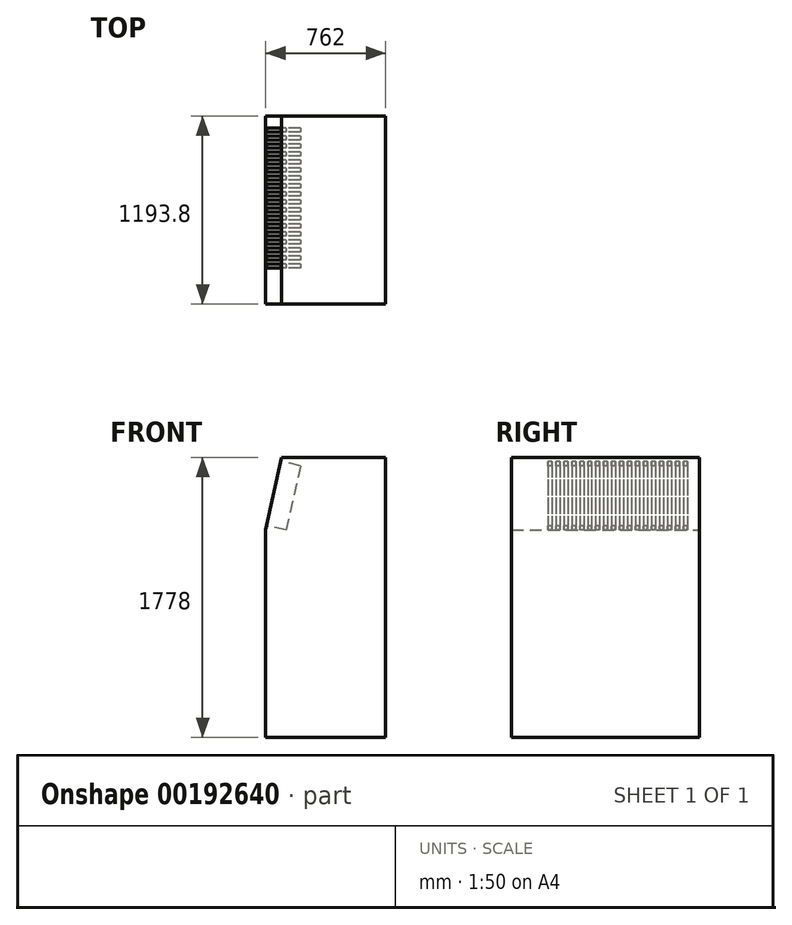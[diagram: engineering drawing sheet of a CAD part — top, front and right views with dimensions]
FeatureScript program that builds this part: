
annotation { "Feature Type Name" : "Feature", "Feature Type Description" : "" }
export const myFeature = defineFeature(function(context is Context, id is Id, definition is map)
    precondition{}
    {
        {
            var Q0;
            Q0=qCreatedBy(makeId("Front.planeOp"),FACE);
            var sketch = newSketch(context, id + "F0", { "sketchPlane" : qUnion([Q0])});
            skLineSegment(sketch, "E0.bottom", {"start": v(-381, 889) * mm, "end": v(381, 889) * mm});
            skLineSegment(sketch, "E0.top", {"start": v(-381, -889) * mm, "end": v(381, -889) * mm});
            skLineSegment(sketch, "E0.left", {"start": v(-381, 889) * mm, "end": v(-381, -889) * mm});
            skLineSegment(sketch, "E0.right", {"start": v(381, 889) * mm, "end": v(381, -889) * mm});
            skSolve(sketch);
        }
        {
            var Q0;
            Q0=makeQuery(id+"F0.imprint","IMPRINT",FACE,{"disambiguationData":[TD([[makeQuery(id+"F0.imprint","IMPRINT",EDGE,{"derivedFrom":sQuery(id+"F0.wireOp",EDGE,"E0.bottom")}),-1.0]])]});
            extrude(context, id + "F1", {"entities" : qUnion([Q0]), "depth" : 1193.8 * mm});
        }
        {
            var Q0;
            Q0=makeQuery(id+"F1.opExtrude","CAP_FACE",FACE,{"disambiguationData":[OSD([sQuery(id+"F0.wireOp",EDGE,"E0.bottom"),sQuery(id+"F0.wireOp",EDGE,"E0.top"),sQuery(id+"F0.wireOp",EDGE,"E0.left"),sQuery(id+"F0.wireOp",EDGE,"E0.right")])],"isStart":true});
            var sketch = newSketch(context, id + "F2", { "sketchPlane" : qUnion([Q0])});
            skLineSegment(sketch, "E1", {"start": v(279.4, 889) * mm, "end": v(381, 430.12) * mm});
            skSolve(sketch);
        }
        {
            var Q0;
            {var subQ0=sQuery(id+"F2.wireOp",EDGE,"E1");Q0=makeQuery(id+"F2.imprint","IMPRINT",FACE,{"disambiguationData":[TD([[makeQuery(id+"F2.imprint","IMPRINT",EDGE,{"derivedFrom":subQ0}),1.0]])]});}
            extrude(context, id + "F3", {"entities" : qUnion([Q0]), "operationType" : NewBodyOperationType.REMOVE, "oppositeDirection" : true, "depth" : 1524 * mm});
        }
        {
            var Q0;
            Q0=makeQuery(id+"F3.boolean.opBoolean","COPY",FACE,{"derivedFrom":makeQuery(id+"F3.opExtrude","SWEPT_FACE",FACE,{"disambiguationData":[OSD([sQuery(id+"F2.wireOp",EDGE,"E1")])]})});
            var sketch = newSketch(context, id + "F4", { "sketchPlane" : qUnion([Q0])});
            skLineSegment(sketch, "E2.bottom", {"start": v(76.2, 782.18) * mm, "end": v(1117.6, 782.18) * mm});
            skLineSegment(sketch, "E2.top", {"start": v(76.2, 362.99) * mm, "end": v(1117.6, 362.99) * mm});
            skLineSegment(sketch, "E2.left", {"start": v(76.2, 782.18) * mm, "end": v(76.2, 362.99) * mm});
            skLineSegment(sketch, "E2.right", {"start": v(1117.6, 782.18) * mm, "end": v(1117.6, 362.99) * mm});
            skLineSegment(sketch, "E3.bottom", {"start": v(101.6, 782.18) * mm, "end": v(127, 782.18) * mm});
            skLineSegment(sketch, "E3.top", {"start": v(101.6, 362.99) * mm, "end": v(127, 362.99) * mm});
            skLineSegment(sketch, "E3.left", {"start": v(101.6, 782.18) * mm, "end": v(101.6, 362.99) * mm});
            skLineSegment(sketch, "E3.right", {"start": v(127, 782.18) * mm, "end": v(127, 362.99) * mm});
            skLineSegment(sketch, "E4.bottom", {"start": v(152.4, 782.18) * mm, "end": v(177.8, 782.18) * mm});
            skLineSegment(sketch, "E4.top", {"start": v(152.4, 362.99) * mm, "end": v(177.8, 362.99) * mm});
            skLineSegment(sketch, "E4.left", {"start": v(152.4, 782.18) * mm, "end": v(152.4, 362.99) * mm});
            skLineSegment(sketch, "E4.right", {"start": v(177.8, 782.18) * mm, "end": v(177.8, 362.99) * mm});
            skLineSegment(sketch, "E5.bottom", {"start": v(203.2, 782.18) * mm, "end": v(228.6, 782.18) * mm});
            skLineSegment(sketch, "E5.top", {"start": v(203.2, 362.99) * mm, "end": v(228.6, 362.99) * mm});
            skLineSegment(sketch, "E5.left", {"start": v(203.2, 782.18) * mm, "end": v(203.2, 362.99) * mm});
            skLineSegment(sketch, "E5.right", {"start": v(228.6, 782.18) * mm, "end": v(228.6, 362.99) * mm});
            skLineSegment(sketch, "E6.bottom", {"start": v(254, 782.18) * mm, "end": v(279.4, 782.18) * mm});
            skLineSegment(sketch, "E6.top", {"start": v(254, 362.99) * mm, "end": v(279.4, 362.99) * mm});
            skLineSegment(sketch, "E6.left", {"start": v(254, 782.18) * mm, "end": v(254, 362.99) * mm});
            skLineSegment(sketch, "E6.right", {"start": v(279.4, 782.18) * mm, "end": v(279.4, 362.99) * mm});
            skLineSegment(sketch, "E7.bottom", {"start": v(304.8, 782.18) * mm, "end": v(330.2, 782.18) * mm});
            skLineSegment(sketch, "E7.top", {"start": v(304.8, 362.99) * mm, "end": v(330.2, 362.99) * mm});
            skLineSegment(sketch, "E7.left", {"start": v(304.8, 782.18) * mm, "end": v(304.8, 362.99) * mm});
            skLineSegment(sketch, "E7.right", {"start": v(330.2, 782.18) * mm, "end": v(330.2, 362.99) * mm});
            skLineSegment(sketch, "E8.bottom", {"start": v(355.6, 782.18) * mm, "end": v(381, 782.18) * mm});
            skLineSegment(sketch, "E8.top", {"start": v(355.6, 362.99) * mm, "end": v(381, 362.99) * mm});
            skLineSegment(sketch, "E8.left", {"start": v(355.6, 782.18) * mm, "end": v(355.6, 362.99) * mm});
            skLineSegment(sketch, "E8.right", {"start": v(381, 782.18) * mm, "end": v(381, 362.99) * mm});
            skLineSegment(sketch, "E9.bottom", {"start": v(406.4, 782.18) * mm, "end": v(431.8, 782.18) * mm});
            skLineSegment(sketch, "E9.top", {"start": v(406.4, 362.99) * mm, "end": v(431.8, 362.99) * mm});
            skLineSegment(sketch, "E9.left", {"start": v(406.4, 782.18) * mm, "end": v(406.4, 362.99) * mm});
            skLineSegment(sketch, "E9.right", {"start": v(431.8, 782.18) * mm, "end": v(431.8, 362.99) * mm});
            skLineSegment(sketch, "E10.bottom", {"start": v(457.2, 782.18) * mm, "end": v(482.6, 782.18) * mm});
            skLineSegment(sketch, "E10.top", {"start": v(457.2, 362.99) * mm, "end": v(482.6, 362.99) * mm});
            skLineSegment(sketch, "E10.left", {"start": v(457.2, 782.18) * mm, "end": v(457.2, 362.99) * mm});
            skLineSegment(sketch, "E10.right", {"start": v(482.6, 782.18) * mm, "end": v(482.6, 362.99) * mm});
            skLineSegment(sketch, "E11.bottom", {"start": v(508, 782.18) * mm, "end": v(533.4, 782.18) * mm});
            skLineSegment(sketch, "E11.top", {"start": v(508, 362.99) * mm, "end": v(533.4, 362.99) * mm});
            skLineSegment(sketch, "E11.left", {"start": v(508, 782.18) * mm, "end": v(508, 362.99) * mm});
            skLineSegment(sketch, "E11.right", {"start": v(533.4, 782.18) * mm, "end": v(533.4, 362.99) * mm});
            skLineSegment(sketch, "E12.bottom", {"start": v(558.8, 782.18) * mm, "end": v(584.2, 782.18) * mm});
            skLineSegment(sketch, "E12.top", {"start": v(558.8, 362.99) * mm, "end": v(584.2, 362.99) * mm});
            skLineSegment(sketch, "E12.left", {"start": v(558.8, 782.18) * mm, "end": v(558.8, 362.99) * mm});
            skLineSegment(sketch, "E12.right", {"start": v(584.2, 782.18) * mm, "end": v(584.2, 362.99) * mm});
            skLineSegment(sketch, "E13.bottom", {"start": v(609.6, 782.18) * mm, "end": v(635, 782.18) * mm});
            skLineSegment(sketch, "E13.top", {"start": v(609.6, 362.99) * mm, "end": v(635, 362.99) * mm});
            skLineSegment(sketch, "E13.left", {"start": v(609.6, 782.18) * mm, "end": v(609.6, 362.99) * mm});
            skLineSegment(sketch, "E13.right", {"start": v(635, 782.18) * mm, "end": v(635, 362.99) * mm});
            skLineSegment(sketch, "E14.bottom", {"start": v(660.4, 782.18) * mm, "end": v(685.8, 782.18) * mm});
            skLineSegment(sketch, "E14.top", {"start": v(660.4, 362.99) * mm, "end": v(685.8, 362.99) * mm});
            skLineSegment(sketch, "E14.left", {"start": v(660.4, 782.18) * mm, "end": v(660.4, 362.99) * mm});
            skLineSegment(sketch, "E14.right", {"start": v(685.8, 782.18) * mm, "end": v(685.8, 362.99) * mm});
            skLineSegment(sketch, "E15.bottom", {"start": v(710.97, 782.18) * mm, "end": v(736.37, 782.18) * mm});
            skLineSegment(sketch, "E15.top", {"start": v(710.97, 362.99) * mm, "end": v(736.37, 362.99) * mm});
            skLineSegment(sketch, "E15.left", {"start": v(710.97, 782.18) * mm, "end": v(710.97, 362.99) * mm});
            skLineSegment(sketch, "E15.right", {"start": v(736.37, 782.18) * mm, "end": v(736.37, 362.99) * mm});
            skLineSegment(sketch, "E16.bottom", {"start": v(761.77, 782.18) * mm, "end": v(787.17, 782.18) * mm});
            skLineSegment(sketch, "E16.top", {"start": v(761.77, 362.99) * mm, "end": v(787.17, 362.99) * mm});
            skLineSegment(sketch, "E16.left", {"start": v(761.77, 782.18) * mm, "end": v(761.77, 362.99) * mm});
            skLineSegment(sketch, "E16.right", {"start": v(787.17, 782.18) * mm, "end": v(787.17, 362.99) * mm});
            skLineSegment(sketch, "E17.bottom", {"start": v(812.57, 782.18) * mm, "end": v(837.97, 782.18) * mm});
            skLineSegment(sketch, "E17.top", {"start": v(812.57, 362.99) * mm, "end": v(837.97, 362.99) * mm});
            skLineSegment(sketch, "E17.left", {"start": v(812.57, 782.18) * mm, "end": v(812.57, 362.99) * mm});
            skLineSegment(sketch, "E17.right", {"start": v(837.97, 782.18) * mm, "end": v(837.97, 362.99) * mm});
            skLineSegment(sketch, "E18.bottom", {"start": v(863.37, 782.18) * mm, "end": v(888.77, 782.18) * mm});
            skLineSegment(sketch, "E18.top", {"start": v(863.37, 362.99) * mm, "end": v(888.77, 362.99) * mm});
            skLineSegment(sketch, "E18.left", {"start": v(863.37, 782.18) * mm, "end": v(863.37, 362.99) * mm});
            skLineSegment(sketch, "E18.right", {"start": v(888.77, 782.18) * mm, "end": v(888.77, 362.99) * mm});
            skLineSegment(sketch, "E19.bottom", {"start": v(914.17, 782.18) * mm, "end": v(939.57, 782.18) * mm});
            skLineSegment(sketch, "E19.top", {"start": v(914.17, 362.99) * mm, "end": v(939.57, 362.99) * mm});
            skLineSegment(sketch, "E19.left", {"start": v(914.17, 782.18) * mm, "end": v(914.17, 362.99) * mm});
            skLineSegment(sketch, "E19.right", {"start": v(939.57, 782.18) * mm, "end": v(939.57, 362.99) * mm});
            skLineSegment(sketch, "E20.bottom", {"start": v(964.97, 782.18) * mm, "end": v(990.37, 782.18) * mm});
            skLineSegment(sketch, "E20.top", {"start": v(964.97, 362.99) * mm, "end": v(990.37, 362.99) * mm});
            skLineSegment(sketch, "E20.left", {"start": v(964.97, 782.18) * mm, "end": v(964.97, 362.99) * mm});
            skLineSegment(sketch, "E20.right", {"start": v(990.37, 782.18) * mm, "end": v(990.37, 362.99) * mm});
            skLineSegment(sketch, "E21.bottom", {"start": v(1005.12, 782.18) * mm, "end": v(1030.52, 782.18) * mm});
            skLineSegment(sketch, "E21.top", {"start": v(1005.12, 362.99) * mm, "end": v(1030.52, 362.99) * mm});
            skLineSegment(sketch, "E21.left", {"start": v(1005.12, 782.18) * mm, "end": v(1005.12, 362.99) * mm});
            skLineSegment(sketch, "E21.right", {"start": v(1030.52, 782.18) * mm, "end": v(1030.52, 362.99) * mm});
            skLineSegment(sketch, "E22.bottom", {"start": v(1055.92, 782.18) * mm, "end": v(1081.32, 782.18) * mm});
            skLineSegment(sketch, "E22.top", {"start": v(1055.92, 362.99) * mm, "end": v(1081.32, 362.99) * mm});
            skLineSegment(sketch, "E22.left", {"start": v(1055.92, 782.18) * mm, "end": v(1055.92, 362.99) * mm});
            skLineSegment(sketch, "E22.right", {"start": v(1081.32, 782.18) * mm, "end": v(1081.32, 362.99) * mm});
            skSolve(sketch);
        }
        {
            var Q0;
            {var subQ0=sQuery(id+"F4.wireOp",EDGE,"E2.left");Q0=makeQuery(id+"F4.imprint","IMPRINT",FACE,{"disambiguationData":[TD([[makeQuery(id+"F4.imprint","IMPRINT",EDGE,{"derivedFrom":subQ0}),1.0]])]});}
            var Q1;
            {var subQ0=sQuery(id+"F4.wireOp",EDGE,"E3.right");Q1=makeQuery(id+"F4.imprint","IMPRINT",FACE,{"disambiguationData":[TD([[makeQuery(id+"F4.imprint","IMPRINT",EDGE,{"derivedFrom":subQ0}),1.0]])]});}
            var Q2;
            {var subQ0=sQuery(id+"F4.wireOp",EDGE,"E4.right");Q2=makeQuery(id+"F4.imprint","IMPRINT",FACE,{"disambiguationData":[TD([[makeQuery(id+"F4.imprint","IMPRINT",EDGE,{"derivedFrom":subQ0}),1.0]])]});}
            var Q3;
            {var subQ0=sQuery(id+"F4.wireOp",EDGE,"E5.right");Q3=makeQuery(id+"F4.imprint","IMPRINT",FACE,{"disambiguationData":[TD([[makeQuery(id+"F4.imprint","IMPRINT",EDGE,{"derivedFrom":subQ0}),1.0]])]});}
            var Q4;
            {var subQ0=sQuery(id+"F4.wireOp",EDGE,"E6.right");Q4=makeQuery(id+"F4.imprint","IMPRINT",FACE,{"disambiguationData":[TD([[makeQuery(id+"F4.imprint","IMPRINT",EDGE,{"derivedFrom":subQ0}),1.0]])]});}
            var Q5;
            {var subQ0=sQuery(id+"F4.wireOp",EDGE,"E7.right");Q5=makeQuery(id+"F4.imprint","IMPRINT",FACE,{"disambiguationData":[TD([[makeQuery(id+"F4.imprint","IMPRINT",EDGE,{"derivedFrom":subQ0}),1.0]])]});}
            var Q6;
            {var subQ0=sQuery(id+"F4.wireOp",EDGE,"E8.right");Q6=makeQuery(id+"F4.imprint","IMPRINT",FACE,{"disambiguationData":[TD([[makeQuery(id+"F4.imprint","IMPRINT",EDGE,{"derivedFrom":subQ0}),1.0]])]});}
            var Q7;
            {var subQ0=sQuery(id+"F4.wireOp",EDGE,"E9.right");Q7=makeQuery(id+"F4.imprint","IMPRINT",FACE,{"disambiguationData":[TD([[makeQuery(id+"F4.imprint","IMPRINT",EDGE,{"derivedFrom":subQ0}),1.0]])]});}
            var Q8;
            {var subQ0=sQuery(id+"F4.wireOp",EDGE,"E10.right");Q8=makeQuery(id+"F4.imprint","IMPRINT",FACE,{"disambiguationData":[TD([[makeQuery(id+"F4.imprint","IMPRINT",EDGE,{"derivedFrom":subQ0}),1.0]])]});}
            var Q9;
            {var subQ0=sQuery(id+"F4.wireOp",EDGE,"E11.right");Q9=makeQuery(id+"F4.imprint","IMPRINT",FACE,{"disambiguationData":[TD([[makeQuery(id+"F4.imprint","IMPRINT",EDGE,{"derivedFrom":subQ0}),1.0]])]});}
            var Q10;
            {var subQ0=sQuery(id+"F4.wireOp",EDGE,"E12.right");Q10=makeQuery(id+"F4.imprint","IMPRINT",FACE,{"disambiguationData":[TD([[makeQuery(id+"F4.imprint","IMPRINT",EDGE,{"derivedFrom":subQ0}),1.0]])]});}
            var Q11;
            {var subQ0=sQuery(id+"F4.wireOp",EDGE,"E13.right");Q11=makeQuery(id+"F4.imprint","IMPRINT",FACE,{"disambiguationData":[TD([[makeQuery(id+"F4.imprint","IMPRINT",EDGE,{"derivedFrom":subQ0}),1.0]])]});}
            var Q12;
            {var subQ0=sQuery(id+"F4.wireOp",EDGE,"E14.right");Q12=makeQuery(id+"F4.imprint","IMPRINT",FACE,{"disambiguationData":[TD([[makeQuery(id+"F4.imprint","IMPRINT",EDGE,{"derivedFrom":subQ0}),1.0]])]});}
            var Q13;
            {var subQ0=sQuery(id+"F4.wireOp",EDGE,"E15.right");Q13=makeQuery(id+"F4.imprint","IMPRINT",FACE,{"disambiguationData":[TD([[makeQuery(id+"F4.imprint","IMPRINT",EDGE,{"derivedFrom":subQ0}),1.0]])]});}
            var Q14;
            {var subQ0=sQuery(id+"F4.wireOp",EDGE,"E16.right");Q14=makeQuery(id+"F4.imprint","IMPRINT",FACE,{"disambiguationData":[TD([[makeQuery(id+"F4.imprint","IMPRINT",EDGE,{"derivedFrom":subQ0}),1.0]])]});}
            var Q15;
            {var subQ0=sQuery(id+"F4.wireOp",EDGE,"E17.right");Q15=makeQuery(id+"F4.imprint","IMPRINT",FACE,{"disambiguationData":[TD([[makeQuery(id+"F4.imprint","IMPRINT",EDGE,{"derivedFrom":subQ0}),1.0]])]});}
            var Q16;
            {var subQ0=sQuery(id+"F4.wireOp",EDGE,"E18.right");Q16=makeQuery(id+"F4.imprint","IMPRINT",FACE,{"disambiguationData":[TD([[makeQuery(id+"F4.imprint","IMPRINT",EDGE,{"derivedFrom":subQ0}),1.0]])]});}
            var Q17;
            {var subQ0=sQuery(id+"F4.wireOp",EDGE,"E19.right");Q17=makeQuery(id+"F4.imprint","IMPRINT",FACE,{"disambiguationData":[TD([[makeQuery(id+"F4.imprint","IMPRINT",EDGE,{"derivedFrom":subQ0}),1.0]])]});}
            var Q18;
            Q18=makeQuery(id+"F4.imprint","IMPRINT",FACE,{"disambiguationData":[TD([[makeQuery(id+"F4.imprint","IMPRINT",EDGE,{"derivedFrom":sQuery(id+"F4.wireOp",EDGE,"E21.bottom")}),-1.0]])]});
            var Q19;
            Q19=makeQuery(id+"F4.imprint","IMPRINT",FACE,{"disambiguationData":[TD([[makeQuery(id+"F4.imprint","IMPRINT",EDGE,{"derivedFrom":sQuery(id+"F4.wireOp",EDGE,"E22.bottom")}),-1.0]])]});
            extrude(context, id + "F5", {"entities" : qUnion([Q0, Q1, Q2, Q3, Q4, Q5, Q6, Q7, Q8, Q9, Q10, Q11, Q12, Q13, Q14, Q15, Q16, Q17, Q18, Q19]), "operationType" : NewBodyOperationType.REMOVE, "oppositeDirection" : true, "depth" : 127 * mm});
        }
    });
